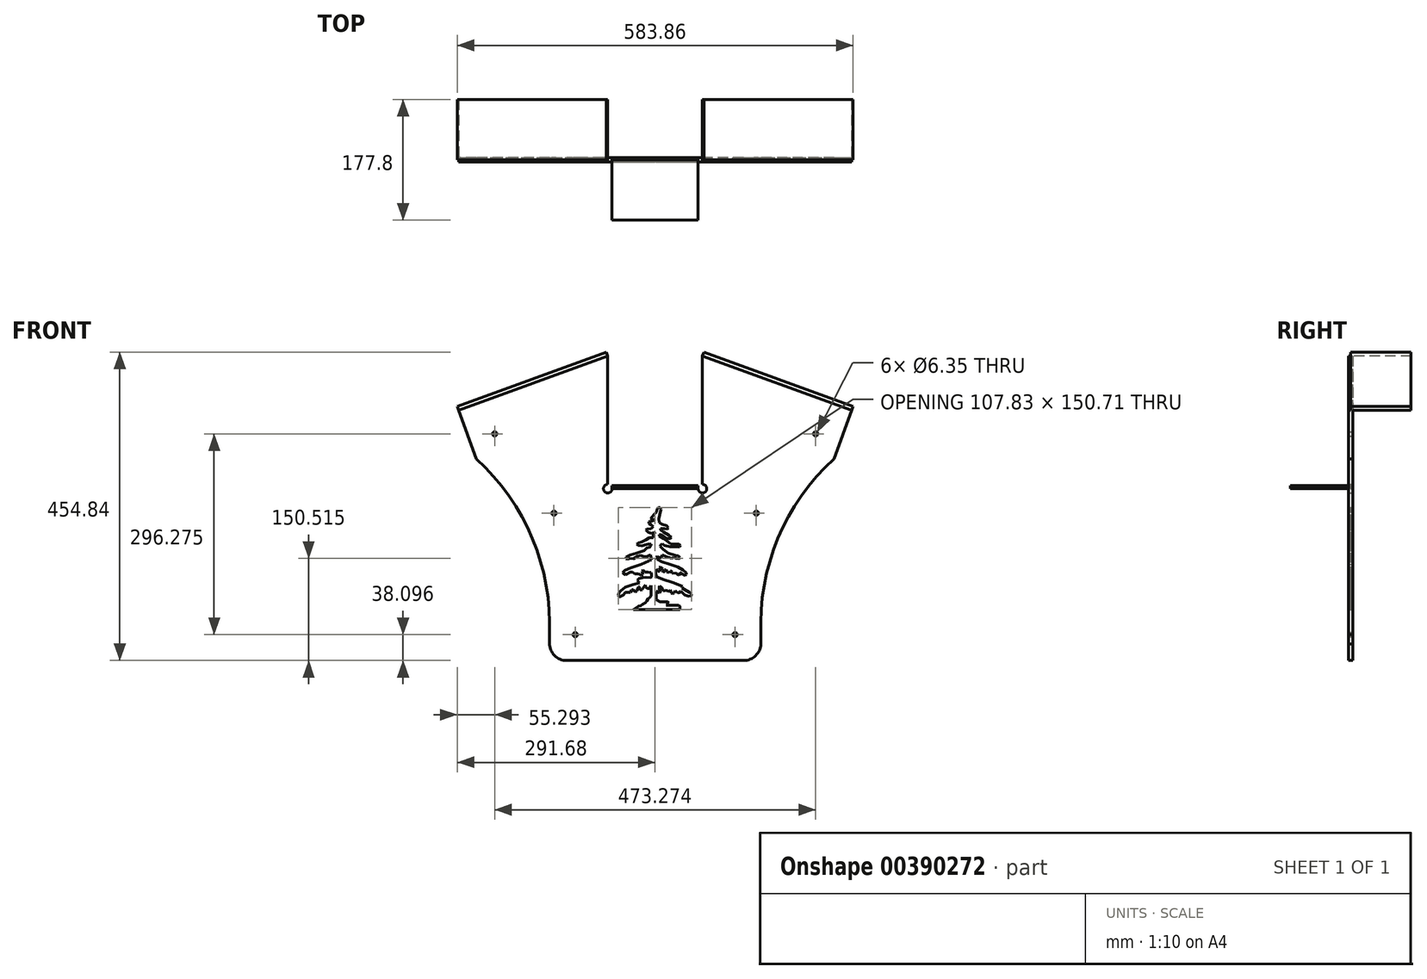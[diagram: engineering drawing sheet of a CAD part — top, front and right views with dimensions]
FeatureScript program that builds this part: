
annotation { "Feature Type Name" : "Feature", "Feature Type Description" : "" }
export const myFeature = defineFeature(function(context is Context, id is Id, definition is map)
    precondition{}
    {
        {
            var Q0;
            Q0=qCreatedBy(makeId("Front.planeOp"),FACE);
            var sketch = newSketch(context, id + "F0", { "sketchPlane" : qUnion([Q0])});
            skLineSegment(sketch, "E0.bottom", {"start": v(-203.2, 255.59) * mm, "end": v(203.2, 255.59) * mm});
            skLineSegment(sketch, "E0.top", {"start": v(-203.2, -255.59) * mm, "end": v(203.2, -255.59) * mm});
            skLineSegment(sketch, "E0.left", {"start": v(-203.2, 255.59) * mm, "end": v(-203.2, -255.59) * mm});
            skLineSegment(sketch, "E0.right", {"start": v(203.2, 255.59) * mm, "end": v(203.2, -255.59) * mm});
            skPoint(sketch, "E0.middle", {"position": v(0, 0) * mm});
            skLineSegment(sketch, "E1", {"start": v(-203.2, 255.59) * mm, "end": v(0, 329.25) * mm});
            skLineSegment(sketch, "E2", {"start": v(0, 329.25) * mm, "end": v(203.2, 255.59) * mm});
            skLineSegment(sketch, "E3", {"start": v(-167.38, -1.62) * mm, "end": v(-203.2, 255.59) * mm});
            skLineSegment(sketch, "E4", {"start": v(-167.38, -1.62) * mm, "end": v(-203.2, -14.6) * mm});
            skLineSegment(sketch, "E5.top", {"start": v(-203.2, -814.39) * mm, "end": v(203.2, -814.39) * mm});
            skLineSegment(sketch, "E5.left", {"start": v(-203.2, -255.59) * mm, "end": v(-203.2, -814.39) * mm});
            skLineSegment(sketch, "E5.right", {"start": v(203.2, -255.59) * mm, "end": v(203.2, -814.39) * mm});
            skLineSegment(sketch, "E6.bottom", {"start": v(-69.85, 348.41) * mm, "end": v(69.85, 348.41) * mm});
            skLineSegment(sketch, "E6.top", {"start": v(-69.85, 113.35) * mm, "end": v(69.85, 113.35) * mm});
            skLineSegment(sketch, "E6.left", {"start": v(-69.85, 348.41) * mm, "end": v(-69.85, 113.35) * mm});
            skLineSegment(sketch, "E6.right", {"start": v(69.85, 348.41) * mm, "end": v(69.85, 113.35) * mm});
            skPoint(sketch, "E6.middle", {"position": v(0, 230.88) * mm});
            skLineSegment(sketch, "E7.top", {"start": v(-69.85, 303.93) * mm, "end": v(69.85, 303.93) * mm});
            skLineSegment(sketch, "E7.left", {"start": v(-69.85, 348.41) * mm, "end": v(-69.85, 303.93) * mm});
            skLineSegment(sketch, "E7.right", {"start": v(69.85, 348.41) * mm, "end": v(69.85, 303.93) * mm});
            skLineSegment(sketch, "E8", {"start": v(-203.2, -255.59) * mm, "end": v(203.2, -319.01) * mm});
            skLineSegment(sketch, "E9", {"start": v(203.2, -255.59) * mm, "end": v(-203.2, -322.39) * mm});
            skLineSegment(sketch, "E10", {"start": v(-203.2, -512.66) * mm, "end": v(203.2, -576.09) * mm});
            skLineSegment(sketch, "E11", {"start": v(203.2, -513) * mm, "end": v(-203.2, -579.8) * mm});
            skLineSegment(sketch, "E12", {"start": v(0, 329.25) * mm, "end": v(-340.45, 205.83) * mm});
            skLineSegment(sketch, "E13", {"start": v(-203.2, -14.6) * mm, "end": v(-289.77, 224.2) * mm});
            skLineSegment(sketch, "E14", {"start": v(0, 329.25) * mm, "end": v(318.78, 213.69) * mm});
            skLineSegment(sketch, "E15", {"start": v(203.2, -144.94) * mm, "end": v(-203.2, -144.94) * mm});
            skLineSegment(sketch, "E16", {"start": v(-203.2, -14.6) * mm, "end": v(-155.95, -144.94) * mm});
            skCircle(sketch, "E17", {"center": v(-236.64, 189.43) * mm, "radius": 3.18 * mm});
            skCircle(sketch, "E18", {"center": v(-149.23, 72.5) * mm, "radius": 3.18 * mm});
            skCircle(sketch, "E19", {"center": v(-117.85, -106.84) * mm, "radius": 3.18 * mm});
            skCircle(sketch, "E20", {"center": v(-100.67, -17.94) * mm, "radius": 3.18 * mm});
            skLineSegment(sketch, "E21", {"start": v(-289.77, 224.2) * mm, "end": v(-291.93, 230.18) * mm});
            skLineSegment(sketch, "E22", {"start": v(-291.93, 230.18) * mm, "end": v(-72.01, 309.9) * mm});
            skLineSegment(sketch, "E23", {"start": v(-72.01, 309.9) * mm, "end": v(-69.85, 303.93) * mm});
            skLineSegment(sketch, "E24", {"start": v(-69.85, 113.35) * mm, "end": v(-69.85, 108.57) * mm});
            skLineSegment(sketch, "E25", {"start": v(-69.85, 108.57) * mm, "end": v(69.85, 108.57) * mm});
            skLineSegment(sketch, "E26", {"start": v(69.85, 108.57) * mm, "end": v(69.85, 113.35) * mm});
            skLineSegment(sketch, "E27", {"start": v(69.85, 303.93) * mm, "end": v(72.01, 309.9) * mm});
            skLineSegment(sketch, "E28", {"start": v(72.01, 309.9) * mm, "end": v(291.93, 230.18) * mm});
            skLineSegment(sketch, "E29", {"start": v(291.93, 230.18) * mm, "end": v(289.77, 224.2) * mm});
            skLineSegment(sketch, "E30", {"start": v(-63.5, 113.35) * mm, "end": v(-63.5, 108.57) * mm});
            skLineSegment(sketch, "E31", {"start": v(63.5, 113.35) * mm, "end": v(63.5, 108.57) * mm});
            skCircle(sketch, "E32", {"center": v(-69.85, 108.57) * mm, "radius": 6.35 * mm});
            skCircle(sketch, "E33", {"center": v(69.85, 108.57) * mm, "radius": 6.35 * mm});
            skCircle(sketch, "E34", {"center": v(0, -106.84) * mm, "radius": 3.18 * mm});
            skCircle(sketch, "E35", {"center": v(117.85, -106.84) * mm, "radius": 3.18 * mm});
            skCircle(sketch, "E36", {"center": v(100.67, -17.94) * mm, "radius": 3.18 * mm});
            skCircle(sketch, "E37", {"center": v(149.23, 72.5) * mm, "radius": 3.18 * mm});
            skCircle(sketch, "E38", {"center": v(236.64, 189.43) * mm, "radius": 3.18 * mm});
            skLineSegment(sketch, "E39", {"start": v(203.2, -14.6) * mm, "end": v(167.38, -1.62) * mm});
            skLineSegment(sketch, "E40", {"start": v(167.38, -1.62) * mm, "end": v(203.2, 255.59) * mm});
            skLineSegment(sketch, "E41", {"start": v(203.2, -14.6) * mm, "end": v(289.77, 224.2) * mm});
            skLineSegment(sketch, "E42", {"start": v(203.2, -14.6) * mm, "end": v(155.95, -144.94) * mm});
            skLineSegment(sketch, "E43", {"start": v(155.95, -144.94) * mm, "end": v(155.95, -106.84) * mm});
            skLineSegment(sketch, "E44", {"start": v(-155.95, -144.94) * mm, "end": v(-155.95, -106.84) * mm});
            skArc(sketch, "E45", {"start": v(-155.95, -106.84) * mm, "mid": v(-180.99, 34.87) * mm, "end": v(-263.8, 152.57) * mm});
            skArc(sketch, "E46", {"start": v(263.8, 152.57) * mm, "mid": v(180.99, 34.87) * mm, "end": v(155.95, -106.84) * mm});
            skLineSegment(sketch, "E47", {"start": v(-27.97, -67.28) * mm, "end": v(36.6, -67.28) * mm});
            skLineSegment(sketch, "E48", {"start": v(36.6, -67.28) * mm, "end": v(36.6, -64.67) * mm});
            skLineSegment(sketch, "E49", {"start": v(36.6, -64.67) * mm, "end": v(34.48, -63.46) * mm});
            skLineSegment(sketch, "E50", {"start": v(34.48, -63.46) * mm, "end": v(16.5, -63.46) * mm});
            skLineSegment(sketch, "E51", {"start": v(18.94, -58.58) * mm, "end": v(7.06, -58.58) * mm});
            skLineSegment(sketch, "E52", {"start": v(7.06, -58.58) * mm, "end": v(1.27, -55.23) * mm});
            skLineSegment(sketch, "E53", {"start": v(1.27, -55.23) * mm, "end": v(1.27, -43.35) * mm});
            skLineSegment(sketch, "E54", {"start": v(1.27, -43.35) * mm, "end": v(3.4, -43.35) * mm});
            skLineSegment(sketch, "E55", {"start": v(3.4, -43.35) * mm, "end": v(6.45, -44.87) * mm});
            skLineSegment(sketch, "E56", {"start": v(6.45, -44.87) * mm, "end": v(8.28, -42.74) * mm});
            skLineSegment(sketch, "E57", {"start": v(8.28, -42.74) * mm, "end": v(6.07, -40.85) * mm});
            skLineSegment(sketch, "E58", {"start": v(6.07, -40.85) * mm, "end": v(6.07, -36.35) * mm});
            skLineSegment(sketch, "E59", {"start": v(6.07, -36.35) * mm, "end": v(6.76, -34.82) * mm});
            skLineSegment(sketch, "E60", {"start": v(6.76, -34.82) * mm, "end": v(9.8, -37.56) * mm});
            skLineSegment(sketch, "E61", {"start": v(9.8, -37.56) * mm, "end": v(11.02, -40.91) * mm});
            skLineSegment(sketch, "E62", {"start": v(11.02, -40.91) * mm, "end": v(11.93, -42.44) * mm});
            skLineSegment(sketch, "E63", {"start": v(11.93, -42.44) * mm, "end": v(14.07, -41.52) * mm});
            skLineSegment(sketch, "E64", {"start": v(17.72, -41.52) * mm, "end": v(18.64, -43.05) * mm});
            skLineSegment(sketch, "E65", {"start": v(18.64, -43.05) * mm, "end": v(20.46, -42.44) * mm});
            skLineSegment(sketch, "E66", {"start": v(20.46, -42.44) * mm, "end": v(22.6, -40.91) * mm});
            skLineSegment(sketch, "E67", {"start": v(22.6, -40.91) * mm, "end": v(23.5, -43.35) * mm});
            skLineSegment(sketch, "E68", {"start": v(23.5, -43.35) * mm, "end": v(23.81, -45.79) * mm});
            skLineSegment(sketch, "E69", {"start": v(23.81, -45.79) * mm, "end": v(26.25, -46.4) * mm});
            skLineSegment(sketch, "E70", {"start": v(26.25, -46.4) * mm, "end": v(27.77, -45.48) * mm});
            skLineSegment(sketch, "E71", {"start": v(27.77, -45.48) * mm, "end": v(28.69, -43.35) * mm});
            skLineSegment(sketch, "E72", {"start": v(28.69, -43.35) * mm, "end": v(29.6, -42.13) * mm});
            skLineSegment(sketch, "E73", {"start": v(29.6, -42.13) * mm, "end": v(31.12, -43.96) * mm});
            skLineSegment(sketch, "E74", {"start": v(31.12, -43.96) * mm, "end": v(33.26, -44.87) * mm});
            skLineSegment(sketch, "E75", {"start": v(33.26, -44.87) * mm, "end": v(34.78, -44.87) * mm});
            skLineSegment(sketch, "E76", {"start": v(34.78, -44.87) * mm, "end": v(37.83, -43.05) * mm});
            skLineSegment(sketch, "E77", {"start": v(37.83, -43.05) * mm, "end": v(39.35, -43.66) * mm});
            skLineSegment(sketch, "E78", {"start": v(39.35, -43.66) * mm, "end": v(43.61, -47.92) * mm});
            skLineSegment(sketch, "E79", {"start": v(43.61, -47.92) * mm, "end": v(49.4, -50.05) * mm});
            skLineSegment(sketch, "E80", {"start": v(49.4, -50.05) * mm, "end": v(52.75, -49.44) * mm});
            skLineSegment(sketch, "E81", {"start": v(52.75, -49.44) * mm, "end": v(53.67, -46.7) * mm});
            skLineSegment(sketch, "E82", {"start": v(53.67, -46.7) * mm, "end": v(50.32, -44.27) * mm});
            skLineSegment(sketch, "E83", {"start": v(50.32, -44.27) * mm, "end": v(41.18, -41.52) * mm});
            skLineSegment(sketch, "E84", {"start": v(41.18, -41.52) * mm, "end": v(37.83, -39.09) * mm});
            skLineSegment(sketch, "E85", {"start": v(37.83, -39.09) * mm, "end": v(39.96, -37.87) * mm});
            skLineSegment(sketch, "E86", {"start": v(39.96, -37.87) * mm, "end": v(40.57, -35.74) * mm});
            skLineSegment(sketch, "E87", {"start": v(40.57, -35.74) * mm, "end": v(25.95, -29.64) * mm});
            skLineSegment(sketch, "E88", {"start": v(25.95, -29.64) * mm, "end": v(11.63, -25.38) * mm});
            skLineSegment(sketch, "E89", {"start": v(11.63, -25.38) * mm, "end": v(4.01, -22.33) * mm});
            skLineSegment(sketch, "E90", {"start": v(4.01, -22.33) * mm, "end": v(1.88, -21.42) * mm});
            skLineSegment(sketch, "E91", {"start": v(1.88, -21.42) * mm, "end": v(0.97, -14.72) * mm});
            skLineSegment(sketch, "E92", {"start": v(0.97, -14.72) * mm, "end": v(1.58, -11.67) * mm});
            skLineSegment(sketch, "E93", {"start": v(1.58, -11.67) * mm, "end": v(1.88, -9.84) * mm});
            skLineSegment(sketch, "E94", {"start": v(1.88, -9.84) * mm, "end": v(4.01, -13.5) * mm});
            skLineSegment(sketch, "E95", {"start": v(4.01, -13.5) * mm, "end": v(6.76, -13.5) * mm});
            skLineSegment(sketch, "E96", {"start": v(6.76, -13.5) * mm, "end": v(7.97, -10.76) * mm});
            skLineSegment(sketch, "E97", {"start": v(7.97, -10.76) * mm, "end": v(5.84, -7.71) * mm});
            skLineSegment(sketch, "E98", {"start": v(5.84, -7.71) * mm, "end": v(7.97, -6.8) * mm});
            skLineSegment(sketch, "E99", {"start": v(7.97, -6.8) * mm, "end": v(11.02, -9.54) * mm});
            skLineSegment(sketch, "E100", {"start": v(11.02, -9.54) * mm, "end": v(10.72, -12.9) * mm});
            skLineSegment(sketch, "E101", {"start": v(10.72, -12.9) * mm, "end": v(11.93, -14.1) * mm});
            skLineSegment(sketch, "E102", {"start": v(11.93, -14.1) * mm, "end": v(14.07, -13.8) * mm});
            skLineSegment(sketch, "E103", {"start": v(14.07, -13.8) * mm, "end": v(14.37, -11.06) * mm});
            skLineSegment(sketch, "E104", {"start": v(14.37, -11.06) * mm, "end": v(15.9, -10.76) * mm});
            skLineSegment(sketch, "E105", {"start": v(15.9, -10.76) * mm, "end": v(17.42, -14.72) * mm});
            skLineSegment(sketch, "E106", {"start": v(17.42, -14.72) * mm, "end": v(20.46, -15.02) * mm});
            skLineSegment(sketch, "E107", {"start": v(20.46, -15.02) * mm, "end": v(21.68, -14.1) * mm});
            skLineSegment(sketch, "E108", {"start": v(21.68, -14.1) * mm, "end": v(21.99, -12.59) * mm});
            skLineSegment(sketch, "E109", {"start": v(21.99, -12.59) * mm, "end": v(25.34, -14.41) * mm});
            skLineSegment(sketch, "E110", {"start": v(25.34, -14.41) * mm, "end": v(25.34, -16.24) * mm});
            skLineSegment(sketch, "E111", {"start": v(25.34, -16.24) * mm, "end": v(30.82, -15.94) * mm});
            skLineSegment(sketch, "E112", {"start": v(30.82, -15.94) * mm, "end": v(32.65, -17.76) * mm});
            skLineSegment(sketch, "E113", {"start": v(32.65, -17.76) * mm, "end": v(35.39, -18.98) * mm});
            skLineSegment(sketch, "E114", {"start": v(36.6, -14.41) * mm, "end": v(39.96, -17.16) * mm});
            skLineSegment(sketch, "E115", {"start": v(39.96, -17.16) * mm, "end": v(43.92, -19.6) * mm});
            skLineSegment(sketch, "E116", {"start": v(43.92, -19.6) * mm, "end": v(45.75, -18.37) * mm});
            skLineSegment(sketch, "E117", {"start": v(45.75, -18.37) * mm, "end": v(45.14, -15.02) * mm});
            skLineSegment(sketch, "E118", {"start": v(45.14, -15.02) * mm, "end": v(40.87, -11.06) * mm});
            skLineSegment(sketch, "E119", {"start": v(40.87, -11.06) * mm, "end": v(33.26, -6.8) * mm});
            skLineSegment(sketch, "E120", {"start": v(33.26, -6.8) * mm, "end": v(21.99, -3.14) * mm});
            skLineSegment(sketch, "E121", {"start": v(21.99, -3.14) * mm, "end": v(10.1, 0.82) * mm});
            skLineSegment(sketch, "E122", {"start": v(10.1, 0.82) * mm, "end": v(3.1, 4.47) * mm});
            skLineSegment(sketch, "E123", {"start": v(3.1, 4.47) * mm, "end": v(1.27, 7.21) * mm});
            skLineSegment(sketch, "E124", {"start": v(1.27, 7.21) * mm, "end": v(3.1, 9.04) * mm});
            skLineSegment(sketch, "E125", {"start": v(3.1, 9.04) * mm, "end": v(5.54, 6.9) * mm});
            skLineSegment(sketch, "E126", {"start": v(5.54, 6.9) * mm, "end": v(9.5, 6.9) * mm});
            skLineSegment(sketch, "E127", {"start": v(9.5, 6.9) * mm, "end": v(9.8, 9.04) * mm});
            skLineSegment(sketch, "E128", {"start": v(9.8, 9.04) * mm, "end": v(10.72, 10.87) * mm});
            skLineSegment(sketch, "E129", {"start": v(10.72, 10.87) * mm, "end": v(16.5, 8.13) * mm});
            skLineSegment(sketch, "E130", {"start": v(16.5, 8.13) * mm, "end": v(20.46, 6.9) * mm});
            skLineSegment(sketch, "E131", {"start": v(20.46, 6.9) * mm, "end": v(23.81, 6) * mm});
            skLineSegment(sketch, "E132", {"start": v(23.81, 6) * mm, "end": v(27.47, 6.9) * mm});
            skLineSegment(sketch, "E133", {"start": v(27.47, 6.9) * mm, "end": v(30.52, 6) * mm});
            skLineSegment(sketch, "E134", {"start": v(30.52, 6) * mm, "end": v(35.08, 5.08) * mm});
            skLineSegment(sketch, "E135", {"start": v(35.08, 5.08) * mm, "end": v(36.6, 6.9) * mm});
            skLineSegment(sketch, "E136", {"start": v(36.6, 6.9) * mm, "end": v(34.17, 9.35) * mm});
            skLineSegment(sketch, "E137", {"start": v(34.17, 9.35) * mm, "end": v(29.3, 10.26) * mm});
            skLineSegment(sketch, "E138", {"start": v(29.3, 10.26) * mm, "end": v(19.24, 13.61) * mm});
            skLineSegment(sketch, "E139", {"start": v(19.24, 13.61) * mm, "end": v(11.63, 19.1) * mm});
            skLineSegment(sketch, "E140", {"start": v(11.63, 19.1) * mm, "end": v(7.37, 23.66) * mm});
            skLineSegment(sketch, "E141", {"start": v(7.37, 23.66) * mm, "end": v(8.28, 26.4) * mm});
            skLineSegment(sketch, "E142", {"start": v(8.28, 26.4) * mm, "end": v(10.41, 27.32) * mm});
            skLineSegment(sketch, "E143", {"start": v(10.41, 27.32) * mm, "end": v(13.76, 24.88) * mm});
            skLineSegment(sketch, "E144", {"start": v(13.76, 24.88) * mm, "end": v(21.68, 22.75) * mm});
            skLineSegment(sketch, "E145", {"start": v(21.68, 22.75) * mm, "end": v(29.9, 22.75) * mm});
            skLineSegment(sketch, "E146", {"start": v(29.9, 22.75) * mm, "end": v(35.7, 22.44) * mm});
            skLineSegment(sketch, "E147", {"start": v(35.7, 22.44) * mm, "end": v(36.91, 24.58) * mm});
            skLineSegment(sketch, "E148", {"start": v(36.91, 24.58) * mm, "end": v(35.39, 26.7) * mm});
            skLineSegment(sketch, "E149", {"start": v(35.39, 26.7) * mm, "end": v(29.6, 27.01) * mm});
            skLineSegment(sketch, "E150", {"start": v(29.6, 27.01) * mm, "end": v(22.3, 27.62) * mm});
            skLineSegment(sketch, "E151", {"start": v(22.3, 27.62) * mm, "end": v(17.11, 31.89) * mm});
            skLineSegment(sketch, "E152", {"start": v(17.11, 31.89) * mm, "end": v(12.24, 34.93) * mm});
            skLineSegment(sketch, "E153", {"start": v(12.24, 34.93) * mm, "end": v(5.84, 38.59) * mm});
            skLineSegment(sketch, "E154", {"start": v(5.84, 38.59) * mm, "end": v(5.84, 40.42) * mm});
            skLineSegment(sketch, "E155", {"start": v(7.97, 40.72) * mm, "end": v(13.15, 37.37) * mm});
            skLineSegment(sketch, "E156", {"start": v(13.15, 37.37) * mm, "end": v(17.42, 35.24) * mm});
            skLineSegment(sketch, "E157", {"start": v(17.42, 35.24) * mm, "end": v(22.3, 35.24) * mm});
            skLineSegment(sketch, "E158", {"start": v(22.3, 35.24) * mm, "end": v(23.81, 36.76) * mm});
            skLineSegment(sketch, "E159", {"start": v(23.81, 36.76) * mm, "end": v(19.85, 40.11) * mm});
            skLineSegment(sketch, "E160", {"start": v(19.85, 40.11) * mm, "end": v(12.54, 44.68) * mm});
            skLineSegment(sketch, "E161", {"start": v(12.54, 44.68) * mm, "end": v(7.67, 47.42) * mm});
            skLineSegment(sketch, "E162", {"start": v(7.67, 47.42) * mm, "end": v(7.67, 49.86) * mm});
            skLineSegment(sketch, "E163", {"start": v(7.67, 49.86) * mm, "end": v(14.37, 49.55) * mm});
            skLineSegment(sketch, "E164", {"start": v(14.37, 49.55) * mm, "end": v(18.33, 49.25) * mm});
            skLineSegment(sketch, "E165", {"start": v(18.33, 49.25) * mm, "end": v(19.24, 51.08) * mm});
            skLineSegment(sketch, "E166", {"start": v(19.24, 51.08) * mm, "end": v(16.8, 54.12) * mm});
            skLineSegment(sketch, "E167", {"start": v(16.8, 54.12) * mm, "end": v(10.72, 56.26) * mm});
            skLineSegment(sketch, "E168", {"start": v(10.72, 56.26) * mm, "end": v(5.84, 58.39) * mm});
            skLineSegment(sketch, "E169", {"start": v(5.84, 58.39) * mm, "end": v(5.23, 64.48) * mm});
            skLineSegment(sketch, "E170", {"start": v(5.23, 64.48) * mm, "end": v(6.45, 69.66) * mm});
            skLineSegment(sketch, "E171", {"start": v(6.45, 69.66) * mm, "end": v(8.28, 77.88) * mm});
            skLineSegment(sketch, "E172", {"start": v(8.28, 77.88) * mm, "end": v(7.06, 80.93) * mm});
            skLineSegment(sketch, "E173", {"start": v(7.06, 80.93) * mm, "end": v(4.93, 80.93) * mm});
            skLineSegment(sketch, "E174", {"start": v(4.93, 80.93) * mm, "end": v(2.8, 79.1) * mm});
            skLineSegment(sketch, "E175", {"start": v(2.8, 79.1) * mm, "end": v(2.5, 74.23) * mm});
            skLineSegment(sketch, "E176", {"start": v(2.5, 74.23) * mm, "end": v(-1.47, 70.27) * mm});
            skLineSegment(sketch, "E177", {"start": v(-1.47, 70.27) * mm, "end": v(-4.82, 66.92) * mm});
            skLineSegment(sketch, "E178", {"start": v(-4.82, 66.92) * mm, "end": v(-6.95, 64.18) * mm});
            skLineSegment(sketch, "E179", {"start": v(-6.95, 64.18) * mm, "end": v(-4.51, 62.96) * mm});
            skLineSegment(sketch, "E180", {"start": v(-4.51, 62.96) * mm, "end": v(-0.55, 63.57) * mm});
            skLineSegment(sketch, "E181", {"start": v(-0.55, 63.57) * mm, "end": v(-1.77, 61.43) * mm});
            skLineSegment(sketch, "E182", {"start": v(-1.77, 61.43) * mm, "end": v(-5.73, 60.52) * mm});
            skLineSegment(sketch, "E183", {"start": v(-5.73, 60.52) * mm, "end": v(-9.39, 59.6) * mm});
            skLineSegment(sketch, "E184", {"start": v(-9.39, 59.6) * mm, "end": v(-9.08, 57.47) * mm});
            skLineSegment(sketch, "E185", {"start": v(-9.08, 57.47) * mm, "end": v(-5.73, 55.34) * mm});
            skLineSegment(sketch, "E186", {"start": v(-5.73, 55.34) * mm, "end": v(-2.69, 52.6) * mm});
            skLineSegment(sketch, "E187", {"start": v(-2.69, 52.6) * mm, "end": v(-6.04, 49.55) * mm});
            skLineSegment(sketch, "E188", {"start": v(-6.04, 49.55) * mm, "end": v(-12.43, 48.95) * mm});
            skLineSegment(sketch, "E189", {"start": v(-12.43, 48.95) * mm, "end": v(-13.65, 47.73) * mm});
            skLineSegment(sketch, "E190", {"start": v(-13.65, 47.73) * mm, "end": v(-10.3, 44.38) * mm});
            skLineSegment(sketch, "E191", {"start": v(-10.3, 44.38) * mm, "end": v(-5.73, 42.55) * mm});
            skLineSegment(sketch, "E192", {"start": v(-5.73, 42.55) * mm, "end": v(-0.86, 43.77) * mm});
            skLineSegment(sketch, "E193", {"start": v(-0.86, 43.77) * mm, "end": v(-0.25, 41.94) * mm});
            skLineSegment(sketch, "E194", {"start": v(-0.25, 41.94) * mm, "end": v(-3, 40.42) * mm});
            skLineSegment(sketch, "E195", {"start": v(-3, 40.42) * mm, "end": v(-3, 36.46) * mm});
            skLineSegment(sketch, "E196", {"start": v(-3, 36.46) * mm, "end": v(-8.78, 36.15) * mm});
            skLineSegment(sketch, "E197", {"start": v(-8.78, 36.15) * mm, "end": v(-13.65, 32.8) * mm});
            skLineSegment(sketch, "E198", {"start": v(-13.65, 32.8) * mm, "end": v(-19.75, 30.06) * mm});
            skLineSegment(sketch, "E199", {"start": v(-19.75, 30.06) * mm, "end": v(-24.62, 28.84) * mm});
            skLineSegment(sketch, "E200", {"start": v(-24.62, 28.84) * mm, "end": v(-26.75, 27.01) * mm});
            skLineSegment(sketch, "E201", {"start": v(-26.75, 27.01) * mm, "end": v(-25.23, 24.58) * mm});
            skLineSegment(sketch, "E202", {"start": v(-25.23, 24.58) * mm, "end": v(-19.75, 24.27) * mm});
            skLineSegment(sketch, "E203", {"start": v(-19.75, 24.27) * mm, "end": v(-13.04, 26.4) * mm});
            skLineSegment(sketch, "E204", {"start": v(-13.04, 26.4) * mm, "end": v(-10.3, 27.01) * mm});
            skLineSegment(sketch, "E205", {"start": v(-10.3, 27.01) * mm, "end": v(-6.34, 26.7) * mm});
            skLineSegment(sketch, "E206", {"start": v(-6.34, 26.7) * mm, "end": v(-5.73, 24.88) * mm});
            skLineSegment(sketch, "E207", {"start": v(-5.73, 24.88) * mm, "end": v(-8.17, 22.44) * mm});
            skLineSegment(sketch, "E208", {"start": v(-8.17, 22.44) * mm, "end": v(-12.13, 20.92) * mm});
            skLineSegment(sketch, "E209", {"start": v(-12.13, 20.92) * mm, "end": v(-16.1, 16.96) * mm});
            skLineSegment(sketch, "E210", {"start": v(-16.1, 16.96) * mm, "end": v(-27.67, 13.61) * mm});
            skLineSegment(sketch, "E211", {"start": v(-27.67, 13.61) * mm, "end": v(-36.2, 11.17) * mm});
            skLineSegment(sketch, "E212", {"start": v(-36.2, 11.17) * mm, "end": v(-42.6, 7.82) * mm});
            skLineSegment(sketch, "E213", {"start": v(-42.6, 7.82) * mm, "end": v(-42.9, 5.39) * mm});
            skLineSegment(sketch, "E214", {"start": v(-42.9, 5.39) * mm, "end": v(-40.15, 4.47) * mm});
            skLineSegment(sketch, "E215", {"start": v(-40.15, 4.47) * mm, "end": v(-37.72, 5.7) * mm});
            skLineSegment(sketch, "E216", {"start": v(-37.72, 5.7) * mm, "end": v(-32.23, 5.39) * mm});
            skLineSegment(sketch, "E217", {"start": v(-32.23, 5.39) * mm, "end": v(-25.53, 8.74) * mm});
            skLineSegment(sketch, "E218", {"start": v(-25.53, 8.74) * mm, "end": v(-21.27, 10.26) * mm});
            skLineSegment(sketch, "E219", {"start": v(-21.27, 10.26) * mm, "end": v(-17, 8.13) * mm});
            skLineSegment(sketch, "E220", {"start": v(-17, 8.13) * mm, "end": v(-12.13, 8.43) * mm});
            skLineSegment(sketch, "E221", {"start": v(-12.13, 8.43) * mm, "end": v(-8.47, 9.96) * mm});
            skLineSegment(sketch, "E222", {"start": v(-8.47, 9.96) * mm, "end": v(-6.95, 10.56) * mm});
            skLineSegment(sketch, "E223", {"start": v(-6.95, 10.56) * mm, "end": v(-5.73, 6.6) * mm});
            skLineSegment(sketch, "E224", {"start": v(-5.73, 6.6) * mm, "end": v(-5.43, 3.56) * mm});
            skLineSegment(sketch, "E225", {"start": v(-5.43, 3.56) * mm, "end": v(-8.47, 2.95) * mm});
            skLineSegment(sketch, "E226", {"start": v(-8.47, 2.95) * mm, "end": v(-9.39, 1.73) * mm});
            skLineSegment(sketch, "E227", {"start": v(-9.39, 1.73) * mm, "end": v(-20.66, -2.84) * mm});
            skLineSegment(sketch, "E228", {"start": v(-20.66, -2.84) * mm, "end": v(-35.89, -8.02) * mm});
            skLineSegment(sketch, "E229", {"start": v(-35.89, -8.02) * mm, "end": v(-45.03, -12.28) * mm});
            skLineSegment(sketch, "E230", {"start": v(-45.03, -12.28) * mm, "end": v(-48.07, -15.02) * mm});
            skLineSegment(sketch, "E231", {"start": v(-48.07, -15.02) * mm, "end": v(-46.86, -16.55) * mm});
            skLineSegment(sketch, "E232", {"start": v(-46.86, -16.55) * mm, "end": v(-43.2, -18.07) * mm});
            skLineSegment(sketch, "E233", {"start": v(-43.2, -18.07) * mm, "end": v(-36.5, -14.72) * mm});
            skLineSegment(sketch, "E234", {"start": v(-36.5, -14.72) * mm, "end": v(-33.45, -14.41) * mm});
            skLineSegment(sketch, "E235", {"start": v(-33.45, -14.41) * mm, "end": v(-30.1, -17.16) * mm});
            skLineSegment(sketch, "E236", {"start": v(-30.1, -17.16) * mm, "end": v(-25.84, -16.85) * mm});
            skLineSegment(sketch, "E237", {"start": v(-25.84, -16.85) * mm, "end": v(-23.4, -17.76) * mm});
            skLineSegment(sketch, "E238", {"start": v(-23.4, -17.76) * mm, "end": v(-20.66, -19.6) * mm});
            skLineSegment(sketch, "E239", {"start": v(-20.66, -19.6) * mm, "end": v(-18.22, -18.07) * mm});
            skLineSegment(sketch, "E240", {"start": v(-18.22, -18.07) * mm, "end": v(-19.44, -13.2) * mm});
            skLineSegment(sketch, "E241", {"start": v(-14.87, -14.41) * mm, "end": v(-10.3, -14.41) * mm});
            skLineSegment(sketch, "E242", {"start": v(-10.3, -14.41) * mm, "end": v(-6.34, -15.02) * mm});
            skLineSegment(sketch, "E243", {"start": v(-6.34, -15.02) * mm, "end": v(-5.12, -18.37) * mm});
            skLineSegment(sketch, "E244", {"start": v(-5.12, -18.37) * mm, "end": v(-5.12, -21.72) * mm});
            skLineSegment(sketch, "E245", {"start": v(-5.12, -21.72) * mm, "end": v(-6.95, -22.64) * mm});
            skLineSegment(sketch, "E246", {"start": v(-6.95, -22.64) * mm, "end": v(-13.35, -22.33) * mm});
            skLineSegment(sketch, "E247", {"start": v(-13.35, -22.33) * mm, "end": v(-18.53, -22.94) * mm});
            skLineSegment(sketch, "E248", {"start": v(-18.53, -22.94) * mm, "end": v(-23.7, -24.16) * mm});
            skLineSegment(sketch, "E249", {"start": v(-23.7, -24.16) * mm, "end": v(-26.14, -26.3) * mm});
            skLineSegment(sketch, "E250", {"start": v(-26.14, -26.3) * mm, "end": v(-24.62, -29.04) * mm});
            skLineSegment(sketch, "E251", {"start": v(-24.62, -29.04) * mm, "end": v(-23.4, -30.56) * mm});
            skLineSegment(sketch, "E252", {"start": v(-23.4, -30.56) * mm, "end": v(-32.54, -32.7) * mm});
            skLineSegment(sketch, "E253", {"start": v(-32.54, -32.7) * mm, "end": v(-44.42, -36.95) * mm});
            skLineSegment(sketch, "E254", {"start": v(-44.42, -36.95) * mm, "end": v(-51.42, -42.44) * mm});
            skLineSegment(sketch, "E255", {"start": v(-51.42, -42.44) * mm, "end": v(-53.56, -45.48) * mm});
            skLineSegment(sketch, "E256", {"start": v(-53.56, -45.48) * mm, "end": v(-54.17, -48.53) * mm});
            skLineSegment(sketch, "E257", {"start": v(-54.17, -48.53) * mm, "end": v(-53.25, -51.27) * mm});
            skLineSegment(sketch, "E258", {"start": v(-53.25, -51.27) * mm, "end": v(-46.86, -48.23) * mm});
            skLineSegment(sketch, "E259", {"start": v(-46.86, -48.23) * mm, "end": v(-44.11, -44.57) * mm});
            skLineSegment(sketch, "E260", {"start": v(-44.11, -44.57) * mm, "end": v(-40.15, -44.27) * mm});
            skLineSegment(sketch, "E261", {"start": v(-40.15, -44.27) * mm, "end": v(-36.2, -44.57) * mm});
            skLineSegment(sketch, "E262", {"start": v(-36.2, -44.57) * mm, "end": v(-34.67, -40.91) * mm});
            skLineSegment(sketch, "E263", {"start": v(-34.67, -40.91) * mm, "end": v(-32.23, -39.7) * mm});
            skLineSegment(sketch, "E264", {"start": v(-32.23, -39.7) * mm, "end": v(-31.63, -41.52) * mm});
            skLineSegment(sketch, "E265", {"start": v(-31.63, -41.52) * mm, "end": v(-29.5, -43.66) * mm});
            skLineSegment(sketch, "E266", {"start": v(-29.5, -43.66) * mm, "end": v(-27.06, -42.74) * mm});
            skLineSegment(sketch, "E267", {"start": v(-27.06, -42.74) * mm, "end": v(-25.84, -38.48) * mm});
            skLineSegment(sketch, "E268", {"start": v(-25.84, -38.48) * mm, "end": v(-24.62, -36.35) * mm});
            skLineSegment(sketch, "E269", {"start": v(-23.1, -38.78) * mm, "end": v(-22.8, -40.91) * mm});
            skLineSegment(sketch, "E270", {"start": v(-22.8, -40.91) * mm, "end": v(-19.44, -40.3) * mm});
            skLineSegment(sketch, "E271", {"start": v(-19.44, -40.3) * mm, "end": v(-18.22, -38.17) * mm});
            skLineSegment(sketch, "E272", {"start": v(-18.22, -38.17) * mm, "end": v(-17, -36.65) * mm});
            skLineSegment(sketch, "E273", {"start": v(-17, -36.65) * mm, "end": v(-15.79, -34.82) * mm});
            skLineSegment(sketch, "E274", {"start": v(-15.79, -34.82) * mm, "end": v(-14.26, -33.3) * mm});
            skLineSegment(sketch, "E275", {"start": v(-14.26, -33.3) * mm, "end": v(-13.96, -37.56) * mm});
            skLineSegment(sketch, "E276", {"start": v(-13.96, -37.56) * mm, "end": v(-11.52, -38.48) * mm});
            skLineSegment(sketch, "E277", {"start": v(-11.52, -38.48) * mm, "end": v(-8.78, -38.48) * mm});
            skLineSegment(sketch, "E278", {"start": v(-8.78, -38.48) * mm, "end": v(-5.73, -34.52) * mm});
            skLineSegment(sketch, "E279", {"start": v(-5.73, -42.44) * mm, "end": v(-6.04, -48.83) * mm});
            skLineSegment(sketch, "E280", {"start": v(-6.04, -48.83) * mm, "end": v(-7.26, -51.58) * mm});
            skLineSegment(sketch, "E281", {"start": v(-7.26, -51.58) * mm, "end": v(-10.3, -53.7) * mm});
            skLineSegment(sketch, "E282", {"start": v(-10.3, -53.7) * mm, "end": v(-12.13, -57.06) * mm});
            skLineSegment(sketch, "E283", {"start": v(-12.13, -57.06) * mm, "end": v(-14.26, -59.5) * mm});
            skLineSegment(sketch, "E284", {"start": v(-14.26, -59.5) * mm, "end": v(-18.83, -61.93) * mm});
            skLineSegment(sketch, "E285", {"start": v(-18.83, -61.93) * mm, "end": v(-20.96, -63.76) * mm});
            skLineSegment(sketch, "E286", {"start": v(-20.96, -63.76) * mm, "end": v(-24.31, -64.67) * mm});
            skLineSegment(sketch, "E287", {"start": v(-24.31, -64.67) * mm, "end": v(-28.27, -67.11) * mm});
            skLineSegment(sketch, "E288", {"start": v(-14.87, -14.41) * mm, "end": v(-17.99, -11.35) * mm});
            skLineSegment(sketch, "E289", {"start": v(-17.99, -11.35) * mm, "end": v(-19.47, -13.03) * mm});
            skLineSegment(sketch, "E290", {"start": v(-23.1, -38.78) * mm, "end": v(-23.1, -35.95) * mm});
            skLineSegment(sketch, "E291", {"start": v(-23.1, -35.95) * mm, "end": v(-24.6, -36.23) * mm});
            skLineSegment(sketch, "E292", {"start": v(-5.73, -34.52) * mm, "end": v(-5.73, -42.44) * mm});
            skLineSegment(sketch, "E293", {"start": v(14.17, -41.37) * mm, "end": v(17.72, -41.52) * mm});
            skLineSegment(sketch, "E294", {"start": v(18.94, -58.58) * mm, "end": v(20.14, -60.2) * mm});
            skLineSegment(sketch, "E295", {"start": v(20.14, -60.2) * mm, "end": v(18.28, -61.31) * mm});
            skLineSegment(sketch, "E296", {"start": v(18.28, -61.31) * mm, "end": v(16.67, -63.3) * mm});
            skLineSegment(sketch, "E297", {"start": v(-28.27, -67.11) * mm, "end": v(-27.97, -67.28) * mm});
            skLineSegment(sketch, "E298", {"start": v(35.39, -18.98) * mm, "end": v(37.1, -17.74) * mm});
            skLineSegment(sketch, "E299", {"start": v(37.1, -17.74) * mm, "end": v(36.63, -14.4) * mm});
            skLineSegment(sketch, "E300", {"start": v(5.84, 40.42) * mm, "end": v(7.97, 40.72) * mm});
            skLineSegment(sketch, "E301", {"start": v(-5.73, 6.6) * mm, "end": v(1.27, 7.21) * mm});
            skLineSegment(sketch, "E302", {"start": v(-5.73, -42.44) * mm, "end": v(1.27, -43.35) * mm});
            skLineSegment(sketch, "E303", {"start": v(-5.12, -18.37) * mm, "end": v(0.97, -14.72) * mm});
            skLineSegment(sketch, "E304", {"start": v(-20.66, -2.84) * mm, "end": v(33.26, -6.8) * mm});
            skLineSegment(sketch, "E305", {"start": v(15.9, -10.76) * mm, "end": v(33.26, -6.8) * mm});
            skLineSegment(sketch, "E306", {"start": v(-17.99, -11.35) * mm, "end": v(-20.66, -2.84) * mm});
            skLineSegment(sketch, "E307", {"start": v(-19.47, -13.03) * mm, "end": v(-19.44, -13.2) * mm});
            skLineSegment(sketch, "E308", {"start": v(37.83, -39.09) * mm, "end": v(37.83, -43.05) * mm});
            skLineSegment(sketch, "E309", {"start": v(11.63, -25.38) * mm, "end": v(6.76, -34.82) * mm});
            skLineSegment(sketch, "E310", {"start": v(-23.1, -35.95) * mm, "end": v(-23.4, -30.56) * mm});
            skLineSegment(sketch, "E311", {"start": v(-5.72, -34.48) * mm, "end": v(-6.95, -22.64) * mm});
            skLineSegment(sketch, "E312", {"start": v(22.6, -40.91) * mm, "end": v(25.95, -29.64) * mm});
            skLineSegment(sketch, "E313", {"start": v(-44.42, -36.95) * mm, "end": v(-36.2, -44.57) * mm});
            skLineSegment(sketch, "E314", {"start": v(-24.6, -36.23) * mm, "end": v(-24.62, -36.35) * mm});
            skLineSegment(sketch, "E315", {"start": v(14.07, -41.52) * mm, "end": v(14.17, -41.37) * mm});
            skLineSegment(sketch, "E316", {"start": v(16.5, -63.46) * mm, "end": v(16.67, -63.3) * mm});
            skLineSegment(sketch, "E317", {"start": v(39.96, -37.87) * mm, "end": v(42.96, -39.8) * mm});
            skLineSegment(sketch, "E318", {"start": v(42.96, -39.8) * mm, "end": v(50.29, -44.1) * mm});
            skLineSegment(sketch, "E319", {"start": v(50.32, -44.27) * mm, "end": v(50.29, -44.1) * mm});
            skLineSegment(sketch, "E320", {"start": v(36.6, -67.28) * mm, "end": v(36.6, -69.78) * mm});
            skLineSegment(sketch, "E321", {"start": v(36.6, -69.78) * mm, "end": v(-31.95, -69.78) * mm});
            skLineSegment(sketch, "E322", {"start": v(-31.95, -69.78) * mm, "end": v(-28.27, -67.11) * mm});
            skArc(sketch, "E323", {"start": v(-155.95, -119.54) * mm, "mid": v(-148.51, -137.5) * mm, "end": v(-130.55, -144.94) * mm});
            skArc(sketch, "E324", {"start": v(130.57, -144.94) * mm, "mid": v(148.84, -137.18) * mm, "end": v(155.95, -118.65) * mm});
            skSolve(sketch);
        }
        {
            var Q0;
            {var subQ1=sQuery(id+"F0.wireOp",EDGE,"E0.bottom");var subQ3=sQuery(id+"F0.wireOp",EDGE,"E6.left");var subQ4=makeQuery(id+"F0.imprint","INTERSECT",VERTEX,{"derivedFrom":[subQ1,subQ3]});Q0=makeQuery(id+"F0.imprint","IMPRINT",FACE,{"disambiguationData":[TD([[makeQuery(id+"F0.imprint","IMPRINT",EDGE,{"disambiguationData":[TD([[subQ4,1.0]])],"derivedFrom":subQ1}),1.0]])]});}
            var Q1;
            {var subQ1=sQuery(id+"F0.wireOp",EDGE,"E0.bottom");var subQ3=sQuery(id+"F0.wireOp",EDGE,"E6.right");var subQ4=makeQuery(id+"F0.imprint","INTERSECT",VERTEX,{"derivedFrom":[subQ1,subQ3]});Q1=makeQuery(id+"F0.imprint","IMPRINT",FACE,{"disambiguationData":[TD([[makeQuery(id+"F0.imprint","IMPRINT",EDGE,{"disambiguationData":[TD([[subQ4,-1.0]])],"derivedFrom":subQ1}),1.0]])]});}
            var Q2;
            {var subQ0=sQuery(id+"F0.wireOp",EDGE,"E3");Q2=makeQuery(id+"F0.imprint","IMPRINT",FACE,{"disambiguationData":[TD([[makeQuery(id+"F0.imprint","IMPRINT",EDGE,{"derivedFrom":subQ0}),1.0]])]});}
            var Q3;
            {var subQ0=sQuery(id+"F0.wireOp",EDGE,"0NorEr0o-LK0v-ndRV-EvyM-FVn7yfBQF9nJ");Q3=makeQuery(id+"F0.imprint","IMPRINT",FACE,{"disambiguationData":[TD([[makeQuery(id+"F0.imprint","IMPRINT",EDGE,{"derivedFrom":subQ0}),1.0]])]});}
            var Q4;
            Q4=makeQuery(id+"F0.imprint","IMPRINT",FACE,{"disambiguationData":[TD([[makeQuery(id+"F0.imprint","IMPRINT",EDGE,{"derivedFrom":sQuery(id+"F0.wireOp",EDGE,"E38")}),-1.0]])]});
            var Q5;
            {var subQ3=sQuery(id+"F0.wireOp",EDGE,"CkrFr4Ka-XNqX-OoZ0-1zal-H5uxqjd8LDBE");var subQ5=sQuery(id+"F0.wireOp",EDGE,"kv3bsJPv-IMs3-Gm7j-kYb6-OrEtLbo6LIeh");var subQ6=makeQuery(id+"F0.imprint","INTERSECT",VERTEX,{"derivedFrom":[subQ5,subQ3]});Q5=makeQuery(id+"F0.imprint","IMPRINT",FACE,{"disambiguationData":[TD([[makeQuery(id+"F0.imprint","IMPRINT",EDGE,{"disambiguationData":[TD([[subQ6,-1.0]])],"derivedFrom":subQ5}),1.0]])]});}
            var Q6;
            Q6=makeQuery(id+"F0.imprint","IMPRINT",FACE,{"disambiguationData":[TD([[makeQuery(id+"F0.imprint","IMPRINT",EDGE,{"derivedFrom":sQuery(id+"F0.wireOp",EDGE,"E17")}),-1.0]])]});
            var Q7;
            {var subQ1=sQuery(id+"F0.wireOp",EDGE,"E0.right");var subQ3=sQuery(id+"F0.wireOp",EDGE,"qmvWcmrc-MJxs-LFjd-3G6s-gt8k63rvKK21");var subQ4=makeQuery(id+"F0.imprint","INTERSECT",VERTEX,{"derivedFrom":[subQ1,subQ3]});Q7=makeQuery(id+"F0.imprint","IMPRINT",FACE,{"disambiguationData":[TD([[makeQuery(id+"F0.imprint","IMPRINT",EDGE,{"disambiguationData":[TD([[subQ4,1.0]])],"derivedFrom":subQ1}),1.0]])]});}
            var Q8;
            {var subQ0=sQuery(id+"F0.wireOp",EDGE,"E40");Q8=makeQuery(id+"F0.imprint","IMPRINT",FACE,{"disambiguationData":[TD([[makeQuery(id+"F0.imprint","IMPRINT",EDGE,{"derivedFrom":subQ0}),-1.0]])]});}
            var Q9;
            {var subQ17=sQuery(id+"F0.wireOp",EDGE,"E3");Q9=makeQuery(id+"F0.imprint","IMPRINT",FACE,{"disambiguationData":[TD([[makeQuery(id+"F0.imprint","IMPRINT",EDGE,{"derivedFrom":subQ17}),-1.0]])]});}
            var Q10;
            Q10=makeQuery(id+"F0.imprint","IMPRINT",FACE,{"disambiguationData":[TD([[makeQuery(id+"F0.imprint","IMPRINT",EDGE,{"derivedFrom":sQuery(id+"F0.wireOp",EDGE,"E20")}),1.0]])]});
            var Q11;
            Q11=makeQuery(id+"F0.imprint","IMPRINT",FACE,{"disambiguationData":[TD([[makeQuery(id+"F0.imprint","IMPRINT",EDGE,{"derivedFrom":sQuery(id+"F0.wireOp",EDGE,"E36")}),1.0]])]});
            var Q12;
            Q12=makeQuery(id+"F0.imprint","IMPRINT",FACE,{"disambiguationData":[TD([[makeQuery(id+"F0.imprint","IMPRINT",EDGE,{"derivedFrom":sQuery(id+"F0.wireOp",EDGE,"E34")}),1.0]])]});
            extrude(context, id + "F1", {"entities" : qUnion([Q0, Q1, Q2, Q3, Q4, Q5, Q6, Q7, Q8, Q9, Q10, Q11, Q12]), "endBound" : BoundingType.SYMMETRIC, "depth" : 6.35 * mm});
        }
        {
            var Q0;
            {var subQ0=sQuery(id+"F0.wireOp",EDGE,"E21");Q0=makeQuery(id+"F0.imprint","IMPRINT",FACE,{"disambiguationData":[TD([[makeQuery(id+"F0.imprint","IMPRINT",EDGE,{"derivedFrom":subQ0}),-1.0]])]});}
            var Q1;
            {var subQ0=sQuery(id+"F0.wireOp",EDGE,"E27");Q1=makeQuery(id+"F0.imprint","IMPRINT",FACE,{"disambiguationData":[TD([[makeQuery(id+"F0.imprint","IMPRINT",EDGE,{"derivedFrom":subQ0}),-1.0]])]});}
            extrude(context, id + "F2", {"entities" : qUnion([Q0, Q1]), "operationType" : NewBodyOperationType.ADD, "oppositeDirection" : true, "depth" : 88.9 * mm});
        }
        {
            var Q0;
            {var subQ0=sQuery(id+"F0.wireOp",EDGE,"E30");Q0=makeQuery(id+"F0.imprint","IMPRINT",FACE,{"disambiguationData":[TD([[makeQuery(id+"F0.imprint","IMPRINT",EDGE,{"derivedFrom":subQ0}),1.0]])]});}
            extrude(context, id + "F3", {"entities" : qUnion([Q0]), "operationType" : NewBodyOperationType.ADD, "depth" : 88.9 * mm});
        }
    });
